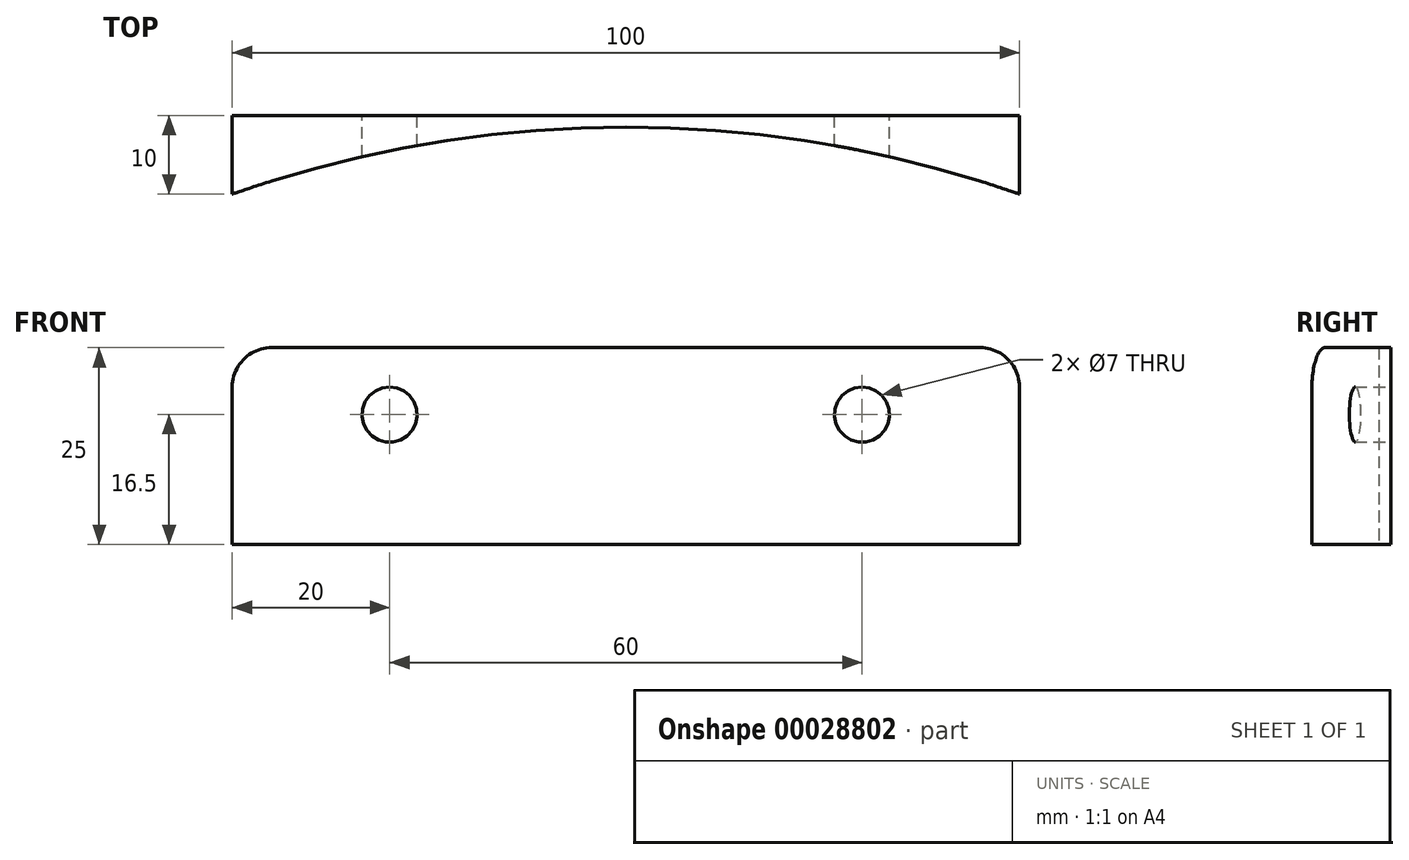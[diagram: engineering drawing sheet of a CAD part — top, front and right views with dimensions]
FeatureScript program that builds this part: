
annotation { "Feature Type Name" : "Feature", "Feature Type Description" : "" }
export const myFeature = defineFeature(function(context is Context, id is Id, definition is map)
    precondition{}
    {
        {
            var Q0;
            Q0=qCreatedBy(makeId("Top.planeOp"),FACE);
            var sketch = newSketch(context, id + "F0", { "sketchPlane" : qUnion([Q0])});
            skLineSegment(sketch, "E0.left", {"start": v(0, 0) * mm, "end": v(0, -8.5) * mm});
            skLineSegment(sketch, "E0.right", {"start": v(-100, 0) * mm, "end": v(-100, -8.5) * mm});
            skLineSegment(sketch, "E1.top", {"start": v(-100, 1.5) * mm, "end": v(0, 1.5) * mm});
            skLineSegment(sketch, "E1.left", {"start": v(-100, 0) * mm, "end": v(-100, 1.5) * mm});
            skLineSegment(sketch, "E1.right", {"start": v(0, -0.5) * mm, "end": v(0, 1.5) * mm});
            skArc(sketch, "E2", {"start": v(0, -8.5) * mm, "mid": v(-50, 0) * mm, "end": v(-100, -8.5) * mm});
            skSolve(sketch);
        }
        {
            var Q0;
            Q0 = qSketchRegion(id + "F0", true);
            extrude(context, id + "F1", {"entities" : qUnion([Q0]), "depth" : 25 * mm});
        }
        {
            var Q0;
            Q0=makeQuery(id+"F1.opExtrude","SWEPT_FACE",FACE,{"disambiguationData":[OSD([sQuery(id+"F0.wireOp",EDGE,"E1.top")])]});
            var sketch = newSketch(context, id + "F2", { "sketchPlane" : qUnion([Q0])});
            skLineSegment(sketch, "E3.0", {"start": v(100, 16.5) * mm, "end": v(0, 16.5) * mm, "construction": true});
            skLineSegment(sketch, "E4.0", {"start": v(20, 25) * mm, "end": v(20, 0) * mm, "construction": true});
            skLineSegment(sketch, "E5.0", {"start": v(80, 25) * mm, "end": v(80, 0) * mm, "construction": true});
            skCircle(sketch, "E6", {"center": v(20, 16.5) * mm, "radius": 3.5 * mm});
            skCircle(sketch, "E7", {"center": v(80, 16.5) * mm, "radius": 3.5 * mm});
            skSolve(sketch);
        }
        {
            var Q0;
            Q0 = qSketchRegion(id + "F2", true);
            extrude(context, id + "F3", {"entities" : qUnion([Q0]), "operationType" : NewBodyOperationType.REMOVE, "oppositeDirection" : true, "depth" : 25 * mm});
        }
        {
            var Q0;
            Q0=makeQuery(id+"F1.opExtrude","CAP_EDGE",EDGE,{"disambiguationData":[OSD([sQuery(id+"F0.wireOp",EDGE,"E0.left"),sQuery(id+"F0.wireOp",EDGE,"E1.right")])],"isStart":false});
            var Q1;
            Q1=makeQuery(id+"F1.opExtrude","CAP_EDGE",EDGE,{"disambiguationData":[OSD([sQuery(id+"F0.wireOp",EDGE,"E0.right"),sQuery(id+"F0.wireOp",EDGE,"E1.left")])],"isStart":false});
            fillet(context, id + "F4", {"entities" : qUnion([Q0, Q1]), "radius" : 5 * mm, "tangentPropagation" : true, "allowEdgeOverflow" : false});
        }
    });
